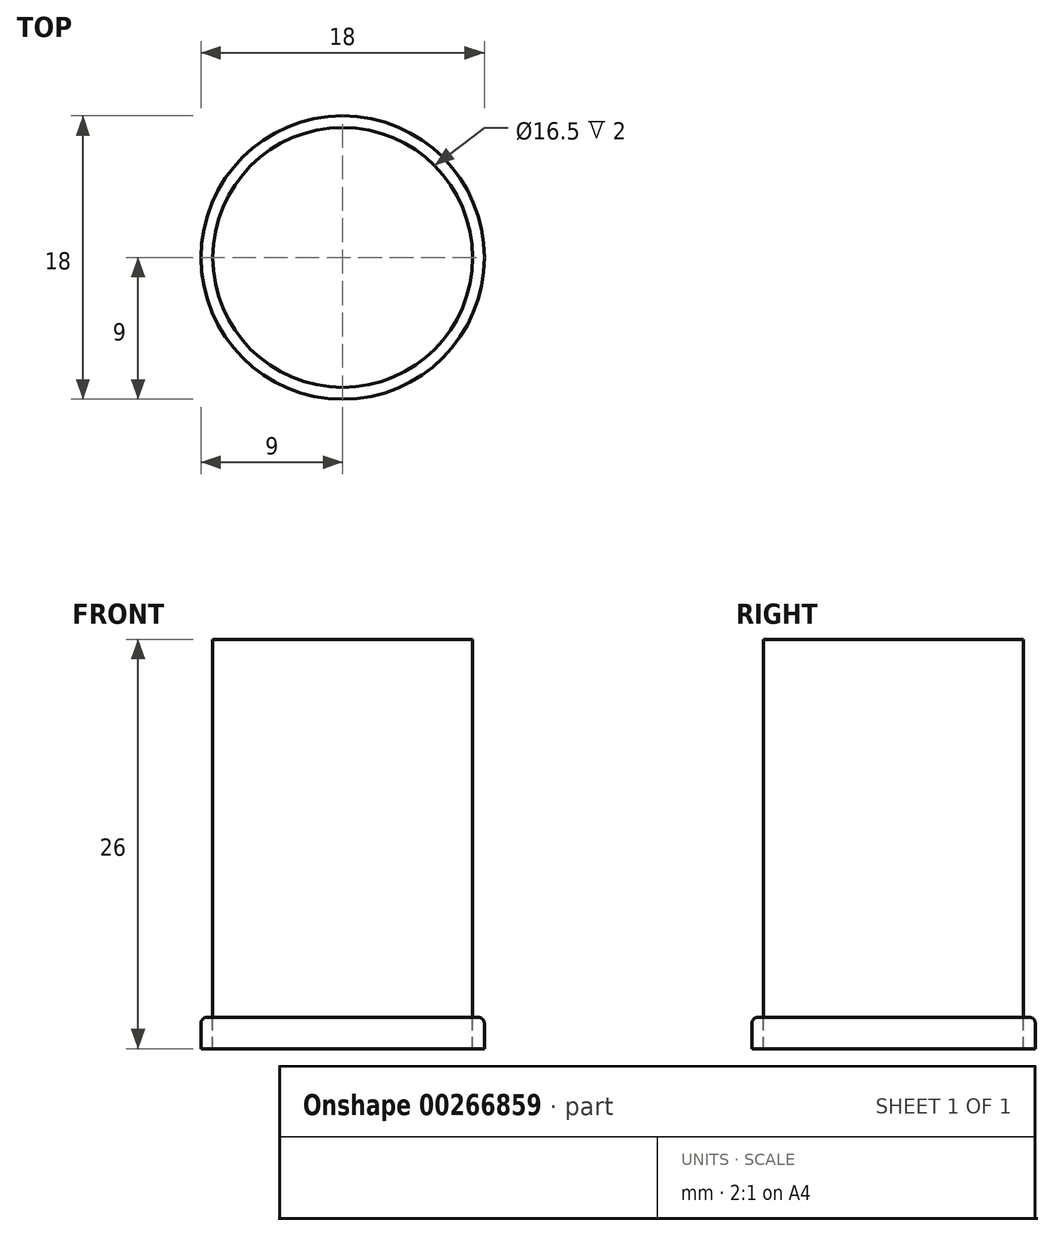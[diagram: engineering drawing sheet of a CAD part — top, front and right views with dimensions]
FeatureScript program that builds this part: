
annotation { "Feature Type Name" : "Feature", "Feature Type Description" : "" }
export const myFeature = defineFeature(function(context is Context, id is Id, definition is map)
    precondition{}
    {
        {
            var Q0;
            Q0=qCreatedBy(makeId("Top.planeOp"),FACE);
            var sketch = newSketch(context, id + "F0", { "sketchPlane" : qUnion([Q0])});
            skCircle(sketch, "E0", {"center": v(0, 0) * mm, "radius": 8.25 * mm});
            skSolve(sketch);
        }
        {
            var Q0;
            Q0 = qSketchRegion(id + "F0", true);
            extrude(context, id + "F1", {"entities" : qUnion([Q0]), "depth" : 24 * mm});
        }
        {
            var Q0;
            Q0=makeQuery(id+"F1.opExtrude","CAP_FACE",FACE,{"disambiguationData":[OSD([sQuery(id+"F0.wireOp",EDGE,"E0")])],"isStart":true});
            var sketch = newSketch(context, id + "F2", { "sketchPlane" : qUnion([Q0])});
            skCircle(sketch, "E1", {"center": v(0, 0) * mm, "radius": 9 * mm});
            skCircle(sketch, "E2", {"center": v(0, 0) * mm, "radius": 8.25 * mm});
            skSolve(sketch);
        }
        {
            var Q0;
            Q0 = qSketchRegion(id + "F2", true);
            extrude(context, id + "F3", {"entities" : qUnion([Q0]), "depth" : 2 * mm});
        }
        {
            var Q0;
            Q0=makeQuery(id+"F3.opExtrude","CAP_EDGE",EDGE,{"disambiguationData":[OSD([sQuery(id+"F2.wireOp",EDGE,"E1")])],"isStart":true});
            fillet(context, id + "F4", {"entities" : qUnion([Q0]), "radius" : 0.4 * mm, "tangentPropagation" : true, "allowEdgeOverflow" : false});
        }
    });
